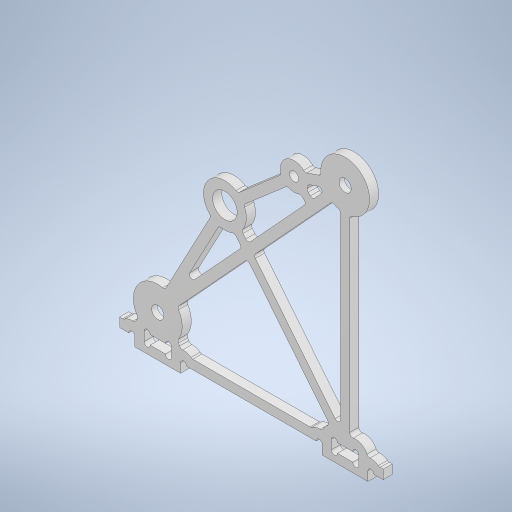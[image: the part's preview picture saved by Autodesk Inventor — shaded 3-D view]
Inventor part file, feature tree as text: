
AUTODESK INVENTOR PART (.ipt)
format: ipt  version: 2023 (Build 270158000, 158)  size: 879,104 bytes
history: native  units: mm
features: extrude x9, sketch x8, other x6, hole x3, fillet x2, projected_geometry x2
ambient origin geometry x8: Origin, YZ Plane, XZ Plane, XY Plane, X Axis, Y Axis, Z Axis, Center Point
bodies: Body1 (feature_tree)
feature tree (30):
  other  "ソリッド1"
  sketch  "スケッチ1"
  extrude  "押し出し1"  Depth=3.0mm
  hole  "穴1"  [1 undecoded]
  hole  "穴2"  [1 undecoded]
  hole  "穴3"  [1 undecoded]
  extrude  "押し出し2"  Depth=3.0mm
  extrude  "押し出し3"  Depth=3.0mm TaperAngle=0.0deg
  fillet  "フィレット1"  Radius=8.0mm
  sketch  "スケッチ4"
  extrude  "押し出し4"  Depth=8.0mm
  extrude  "押し出し5"  Depth=0.7mm TaperAngle=0.0deg
  extrude  "押し出し6"  Depth=3.0mm
  fillet  "フィレット2"  Radius=3.0mm
  extrude  "押し出し7"  Depth=3.0mm TaperAngle=0.0deg
  extrude  "押し出し8"  Depth=1.0mm
  extrude  "押し出し9"  Depth=15.0mm
  sketch  "スケッチ2"
  sketch  "スケッチ3"
  sketch  "スケッチ5"
  projected_geometry  "投影ループ1"
  sketch  "スケッチ6"
  projected_geometry  "投影ループ2"
  sketch  "スケッチ7"
  sketch  "スケッチ8"
  other  "断面エッジを投影1"
  other  "断面エッジを投影2"
  other  "断面エッジを投影3"
  other  "断面エッジを投影4"
  other  "断面エッジを投影5"
note: 3 required parameter values undecoded (feature->parameter linkage not recoverable at this tier; creation-order binding heuristic only, values carry confidence <= 0.55)
